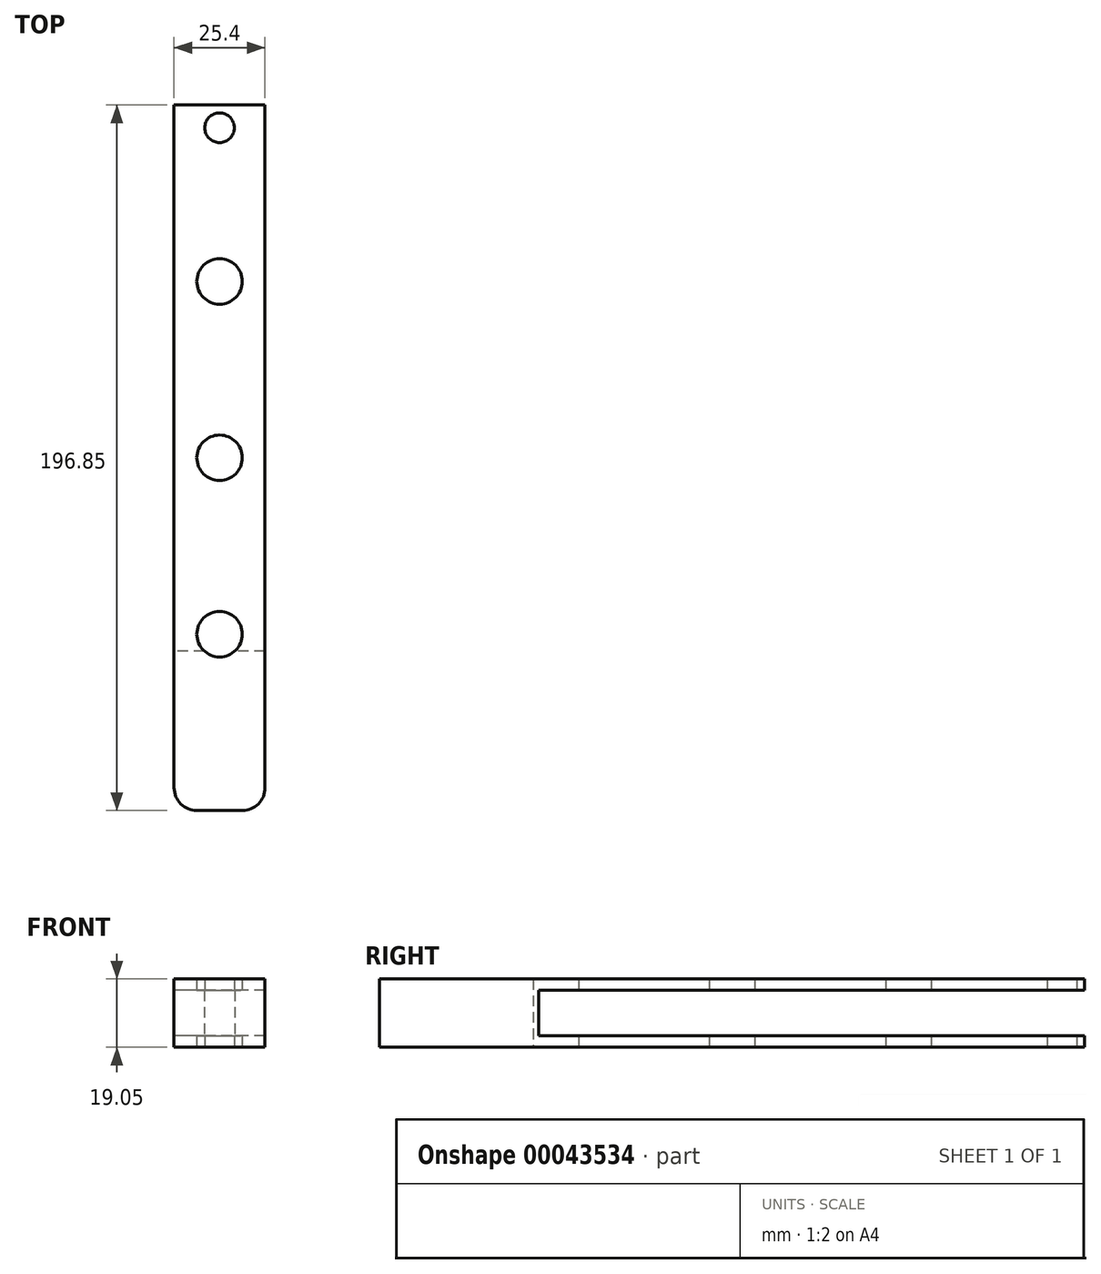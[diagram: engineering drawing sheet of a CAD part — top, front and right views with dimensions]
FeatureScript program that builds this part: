
annotation { "Feature Type Name" : "Feature", "Feature Type Description" : "" }
export const myFeature = defineFeature(function(context is Context, id is Id, definition is map)
    precondition{}
    {
        {
            var Q0;
            Q0=qCreatedBy(makeId("Top.planeOp"),FACE);
            var sketch = newSketch(context, id + "F0", { "sketchPlane" : qUnion([Q0])});
            skPoint(sketch, "E0", {"position": v(0, 196.85) * mm});
            skPoint(sketch, "E1", {"position": v(25.4, 196.85) * mm});
            skLineSegment(sketch, "E2.bottom", {"start": v(25.4, 196.85) * mm, "end": v(6.35, 196.85) * mm});
            skLineSegment(sketch, "E2.top", {"start": v(19.05, 0) * mm, "end": v(6.35, 0) * mm});
            skLineSegment(sketch, "E2.left", {"start": v(25.4, 196.85) * mm, "end": v(25.4, 6.35) * mm});
            skLineSegment(sketch, "E2.right", {"start": v(0, 196.85) * mm, "end": v(0, 0) * mm});
            skPoint(sketch, "E3", {"position": v(12.7, 98.43) * mm});
            skPoint(sketch, "E3.positionSnap0", {"position": v(0, 98.43) * mm});
            skPoint(sketch, "E3.positionSnap1", {"position": v(12.7, 196.85) * mm});
            skLineSegment(sketch, "E4", {"start": v(0, 190.5) * mm, "end": v(0, 98.43) * mm});
            skLineSegment(sketch, "E5", {"start": v(0, 98.43) * mm, "end": v(0, 6.35) * mm});
            skPoint(sketch, "E6", {"position": v(0, 49.21) * mm});
            skPoint(sketch, "E7", {"position": v(0, 147.64) * mm});
            skPoint(sketch, "E8", {"position": v(12.7, 147.64) * mm});
            skPoint(sketch, "E9", {"position": v(12.7, 49.21) * mm});
            skPoint(sketch, "E9.positionSnap0", {"position": v(12.7, 0) * mm});
            skPoint(sketch, "E10.visualSharp", {"position": v(25.4, 0) * mm});
            skArc(sketch, "E10.filletArc", {"start": v(19.05, 0) * mm, "mid": v(23.54, 1.86) * mm, "end": v(25.4, 6.35) * mm});
            skPoint(sketch, "E11.visualSharp", {"position": v(0, 0) * mm});
            skArc(sketch, "E11.filletArc", {"start": v(0, 6.35) * mm, "mid": v(1.86, 1.86) * mm, "end": v(6.35, 0) * mm});
            skPoint(sketch, "E12", {"position": v(12.7, 141.29) * mm});
            skPoint(sketch, "E13", {"position": v(12.7, 104.78) * mm});
            skPoint(sketch, "E14", {"position": v(12.7, 55.56) * mm});
            skCircle(sketch, "E15", {"center": v(12.7, 49.21) * mm, "radius": 6.35 * mm});
            skCircle(sketch, "E16", {"center": v(12.7, 98.43) * mm, "radius": 6.35 * mm});
            skCircle(sketch, "E17", {"center": v(12.7, 147.64) * mm, "radius": 6.35 * mm});
            skPoint(sketch, "E18", {"position": v(12.7, 190.5) * mm});
            skPoint(sketch, "E19", {"position": v(12.7, 186.36) * mm});
            skCircle(sketch, "E20", {"center": v(12.7, 190.5) * mm, "radius": 4.14 * mm});
            skLineSegment(sketch, "E21", {"start": v(6.35, 196.85) * mm, "end": v(0, 196.85) * mm});
            skSolve(sketch);
        }
        {
            var Q0;
            Q0 = qSketchRegion(id + "F0", true);
            extrude(context, id + "F1", {"entities" : qUnion([Q0]), "depth" : 19.05 * mm});
        }
        {
            var Q0;
            Q0=makeQuery(id+"F1.opExtrude","SWEPT_FACE",FACE,{"disambiguationData":[OSD([sQuery(id+"F0.wireOp",EDGE,"E2.bottom")])]});
            var sketch = newSketch(context, id + "F2", { "sketchPlane" : qUnion([Q0])});
            skPoint(sketch, "E22", {"position": v(-12.7, 15.88) * mm});
            skPoint(sketch, "E23", {"position": v(-25.4, 15.88) * mm});
            skPoint(sketch, "E24", {"position": v(-12.7, 3.17) * mm});
            skLineSegment(sketch, "E25.bottom", {"start": v(-25.4, 15.88) * mm, "end": v(-12.7, 15.88) * mm});
            skLineSegment(sketch, "E25.top", {"start": v(-25.4, 3.17) * mm, "end": v(-12.7, 3.17) * mm});
            skLineSegment(sketch, "E25.left", {"start": v(-25.4, 15.88) * mm, "end": v(-25.4, 3.17) * mm});
            skLineSegment(sketch, "E25.right", {"start": v(-12.7, 15.88) * mm, "end": v(-12.7, 3.17) * mm});
            skLineSegment(sketch, "E26.bottom", {"start": v(-12.7, 15.88) * mm, "end": v(0, 15.88) * mm});
            skLineSegment(sketch, "E26.top", {"start": v(-12.7, 3.18) * mm, "end": v(0, 3.18) * mm});
            skLineSegment(sketch, "E26.left", {"start": v(-12.7, 15.88) * mm, "end": v(-12.7, 3.18) * mm});
            skLineSegment(sketch, "E26.right", {"start": v(0, 15.88) * mm, "end": v(0, 3.18) * mm});
            skSolve(sketch);
        }
        {
            var Q0;
            Q0 = qSketchRegion(id + "F2", true);
            extrude(context, id + "F3", {"entities" : qUnion([Q0]), "operationType" : NewBodyOperationType.REMOVE, "oppositeDirection" : true, "depth" : 152.4 * mm});
        }
    });
